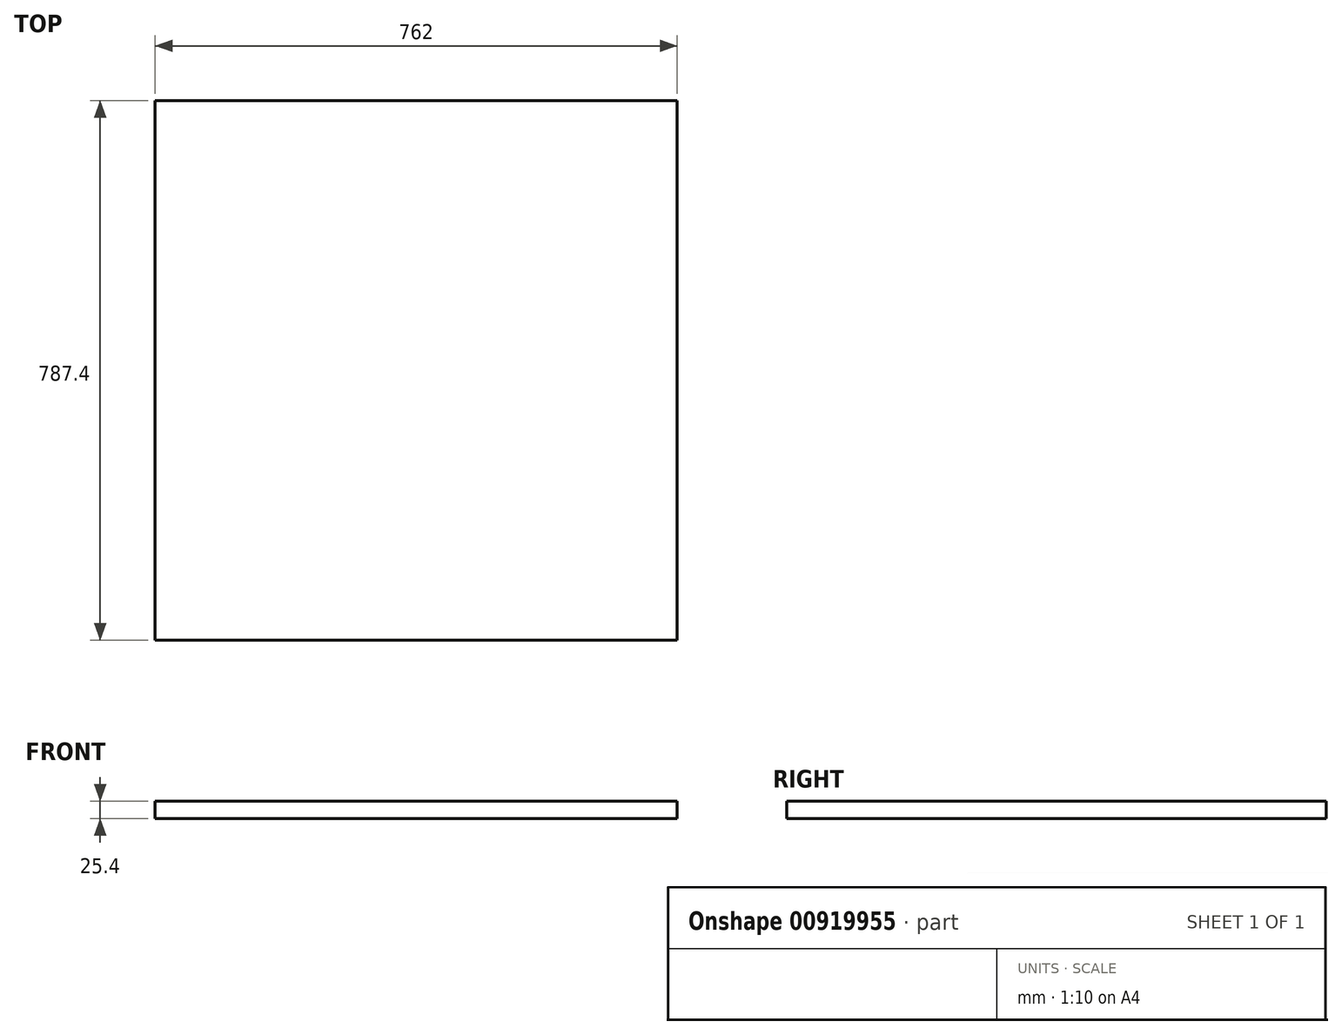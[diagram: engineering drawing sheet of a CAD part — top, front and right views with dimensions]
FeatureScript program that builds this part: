
annotation { "Feature Type Name" : "Feature", "Feature Type Description" : "" }
export const myFeature = defineFeature(function(context is Context, id is Id, definition is map)
    precondition{}
    {
        {
            var Q0;
            Q0=qCreatedBy(makeId("Top.planeOp"),FACE);
            var sketch = newSketch(context, id + "F0", { "sketchPlane" : qUnion([Q0])});
            skLineSegment(sketch, "E0.bottom", {"start": v(381, -393.7) * mm, "end": v(-381, -393.7) * mm});
            skLineSegment(sketch, "E0.top", {"start": v(381, 393.7) * mm, "end": v(-381, 393.7) * mm});
            skLineSegment(sketch, "E0.left", {"start": v(381, -393.7) * mm, "end": v(381, 393.7) * mm});
            skLineSegment(sketch, "E0.right", {"start": v(-381, -393.7) * mm, "end": v(-381, 393.7) * mm});
            skPoint(sketch, "E0.middle", {"position": v(0, 0) * mm});
            skSolve(sketch);
        }
        {
            var Q0;
            Q0=makeQuery(id+"F0.imprint","IMPRINT",FACE,{"disambiguationData":[TD([[makeQuery(id+"F0.imprint","IMPRINT",EDGE,{"derivedFrom":sQuery(id+"F0.wireOp",EDGE,"E0.bottom")}),-1.0]])]});
            extrude(context, id + "F1", {"entities" : qUnion([Q0]), "depth" : 25.4 * mm, "offsetDistance" : 25.4 * mm});
        }
    });
